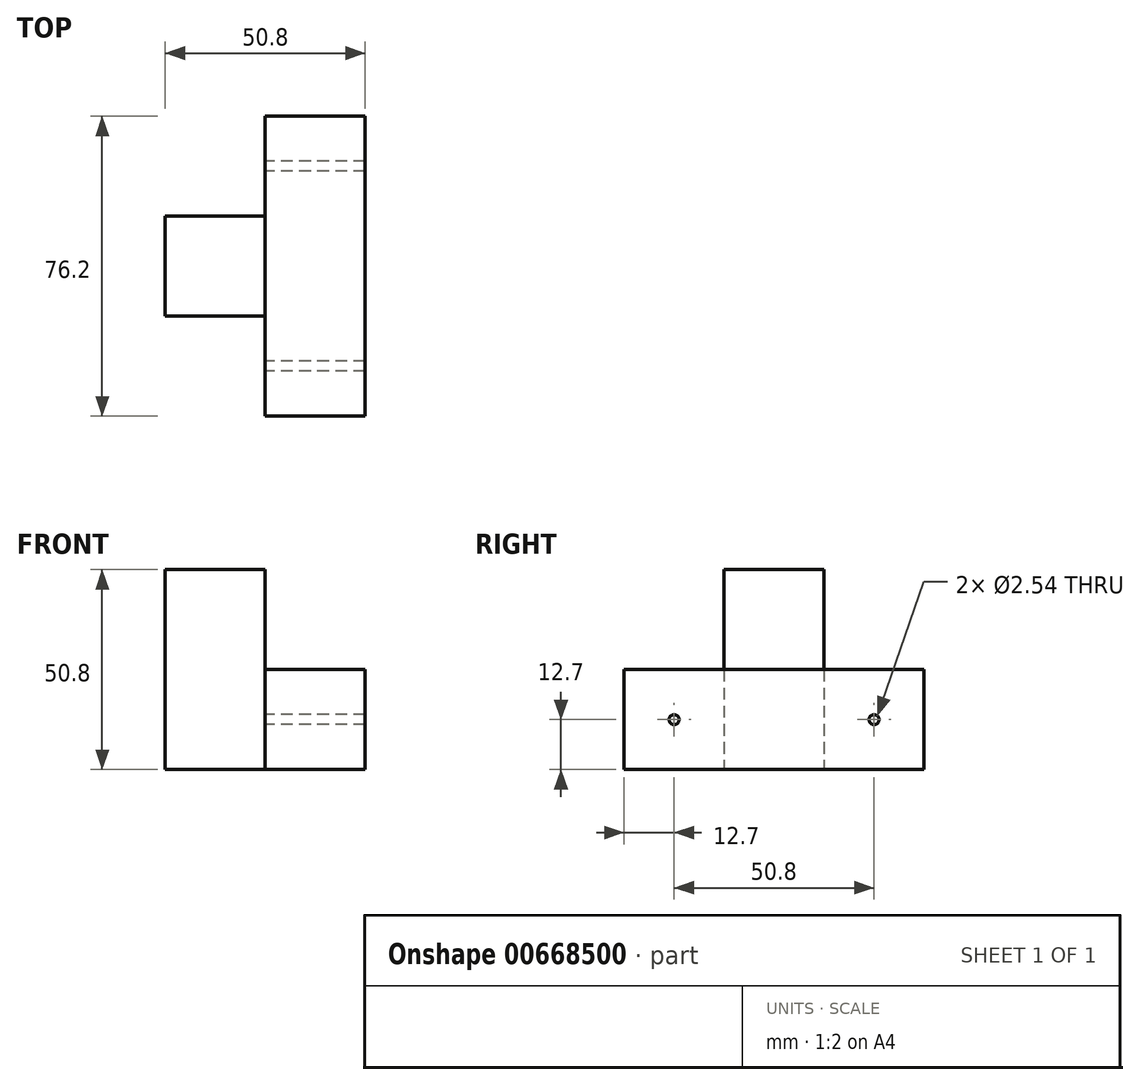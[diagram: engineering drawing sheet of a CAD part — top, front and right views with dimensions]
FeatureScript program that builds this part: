
annotation { "Feature Type Name" : "Feature", "Feature Type Description" : "" }
export const myFeature = defineFeature(function(context is Context, id is Id, definition is map)
    precondition{}
    {
        {
            var Q0;
            Q0=qCreatedBy(makeId("Front.planeOp"),FACE);
            var sketch = newSketch(context, id + "F0", { "sketchPlane" : qUnion([Q0])});
            skLineSegment(sketch, "E0.bottom", {"start": v(0, 0) * mm, "end": v(-25.4, 0) * mm});
            skLineSegment(sketch, "E0.top", {"start": v(0, 25.4) * mm, "end": v(-25.4, 25.4) * mm});
            skLineSegment(sketch, "E0.left", {"start": v(0, 0) * mm, "end": v(0, 25.4) * mm});
            skLineSegment(sketch, "E0.right", {"start": v(-25.4, 0) * mm, "end": v(-25.4, 25.4) * mm});
            skLineSegment(sketch, "E1.bottom", {"start": v(-25.4, 0) * mm, "end": v(-50.8, 0) * mm});
            skLineSegment(sketch, "E1.top", {"start": v(-25.4, 50.8) * mm, "end": v(-50.8, 50.8) * mm});
            skLineSegment(sketch, "E1.left", {"start": v(-25.4, 0) * mm, "end": v(-25.4, 50.8) * mm});
            skLineSegment(sketch, "E1.right", {"start": v(-50.8, 0) * mm, "end": v(-50.8, 50.8) * mm});
            skSolve(sketch);
        }
        {
            var Q0;
            {var subQ3=sQuery(id+"F0.wireOp",EDGE,"E1.bottom");Q0=makeQuery(id+"F0.imprint","IMPRINT",FACE,{"disambiguationData":[TD([[makeQuery(id+"F0.imprint","IMPRINT",EDGE,{"derivedFrom":subQ3}),-1.0]])]});}
            var Q1;
            {var subQ0=sQuery(id+"F0.wireOp",EDGE,"E0.bottom");Q1=makeQuery(id+"F0.imprint","IMPRINT",FACE,{"disambiguationData":[TD([[makeQuery(id+"F0.imprint","IMPRINT",EDGE,{"derivedFrom":subQ0}),-1.0]])]});}
            extrude(context, id + "F1", {"entities" : qUnion([Q0, Q1]), "depth" : 25.4 * mm, "offsetDistance" : 25.4 * mm});
        }
        {
            var Q0;
            Q0=makeQuery(id+"F1.opExtrude","CAP_FACE",FACE,{"disambiguationData":[OSD([sQuery(id+"F0.wireOp",EDGE,"E0.bottom"),sQuery(id+"F0.wireOp",EDGE,"E0.top"),sQuery(id+"F0.wireOp",EDGE,"E0.left"),sQuery(id+"F0.wireOp",EDGE,"E1.bottom"),sQuery(id+"F0.wireOp",EDGE,"E1.top"),sQuery(id+"F0.wireOp",EDGE,"E1.left"),sQuery(id+"F0.wireOp",EDGE,"E1.right")])],"isStart":false});
            var sketch = newSketch(context, id + "F2", { "sketchPlane" : qUnion([Q0])});
            skLineSegment(sketch, "E2.bottom", {"start": v(-25.4, 25.4) * mm, "end": v(0, 25.4) * mm});
            skLineSegment(sketch, "E2.top", {"start": v(-25.4, 0) * mm, "end": v(0, 0) * mm});
            skLineSegment(sketch, "E2.left", {"start": v(-25.4, 25.4) * mm, "end": v(-25.4, 0) * mm});
            skLineSegment(sketch, "E2.right", {"start": v(0, 25.4) * mm, "end": v(0, 0) * mm});
            skSolve(sketch);
        }
        {
            var Q0;
            Q0=makeQuery(id+"F2.imprint","IMPRINT",FACE,{"disambiguationData":[TD([[makeQuery(id+"F2.imprint","IMPRINT",EDGE,{"derivedFrom":sQuery(id+"F2.wireOp",EDGE,"E2.bottom")}),1.0]])]});
            extrude(context, id + "F3", {"entities" : qUnion([Q0]), "operationType" : NewBodyOperationType.ADD, "depth" : 25.4 * mm, "offsetDistance" : 25.4 * mm});
        }
        {
            var Q0;
            Q0=makeQuery(id+"F1.opExtrude","CAP_FACE",FACE,{"disambiguationData":[OSD([sQuery(id+"F0.wireOp",EDGE,"E0.bottom"),sQuery(id+"F0.wireOp",EDGE,"E0.top"),sQuery(id+"F0.wireOp",EDGE,"E0.left"),sQuery(id+"F0.wireOp",EDGE,"E1.bottom"),sQuery(id+"F0.wireOp",EDGE,"E1.top"),sQuery(id+"F0.wireOp",EDGE,"E1.left"),sQuery(id+"F0.wireOp",EDGE,"E1.right")])],"isStart":true});
            var sketch = newSketch(context, id + "F4", { "sketchPlane" : qUnion([Q0])});
            skLineSegment(sketch, "E3.bottom", {"start": v(0, 25.4) * mm, "end": v(25.4, 25.4) * mm});
            skLineSegment(sketch, "E3.top", {"start": v(0, 0) * mm, "end": v(25.4, 0) * mm});
            skLineSegment(sketch, "E3.left", {"start": v(0, 25.4) * mm, "end": v(0, 0) * mm});
            skLineSegment(sketch, "E3.right", {"start": v(25.4, 25.4) * mm, "end": v(25.4, 0) * mm});
            skSolve(sketch);
        }
        {
            var Q0;
            Q0=makeQuery(id+"F4.imprint","IMPRINT",FACE,{"disambiguationData":[TD([[makeQuery(id+"F4.imprint","IMPRINT",EDGE,{"derivedFrom":sQuery(id+"F4.wireOp",EDGE,"E3.bottom")}),-1.0]])]});
            extrude(context, id + "F5", {"entities" : qUnion([Q0]), "operationType" : NewBodyOperationType.ADD, "depth" : 25.4 * mm, "offsetDistance" : 25.4 * mm});
        }
        {
            var Q0;
            Q0=makeQuery(id+"F5.opExtrude","SWEPT_FACE",FACE,{"disambiguationData":[OSD([sQuery(id+"F4.wireOp",EDGE,"E3.right")])]});
            var sketch = newSketch(context, id + "F6", { "sketchPlane" : qUnion([Q0])});
            skCircle(sketch, "E4", {"center": v(-12.7, 12.7) * mm, "radius": 1.27 * mm});
            skSolve(sketch);
        }
        {
            var Q0;
            Q0=makeQuery(id+"F3.opExtrude","SWEPT_FACE",FACE,{"disambiguationData":[OSD([sQuery(id+"F2.wireOp",EDGE,"E2.left")])]});
            var sketch = newSketch(context, id + "F7", { "sketchPlane" : qUnion([Q0])});
            skCircle(sketch, "E5", {"center": v(38.1, 12.7) * mm, "radius": 1.27 * mm});
            skSolve(sketch);
        }
        {
            var Q0;
            Q0=makeQuery(id+"F7.imprint","IMPRINT",FACE,{"disambiguationData":[TD([[makeQuery(id+"F7.imprint","IMPRINT",EDGE,{"derivedFrom":sQuery(id+"F7.wireOp",EDGE,"E5")}),1.0]])]});
            var Q1;
            Q1=makeQuery(id+"F6.imprint","IMPRINT",FACE,{"disambiguationData":[TD([[makeQuery(id+"F6.imprint","IMPRINT",EDGE,{"derivedFrom":sQuery(id+"F6.wireOp",EDGE,"E4")}),1.0]])]});
            extrude(context, id + "F8", {"entities" : qUnion([Q0, Q1]), "operationType" : NewBodyOperationType.REMOVE, "oppositeDirection" : true, "depth" : 25.4 * mm, "offsetDistance" : 25.4 * mm});
        }
    });
